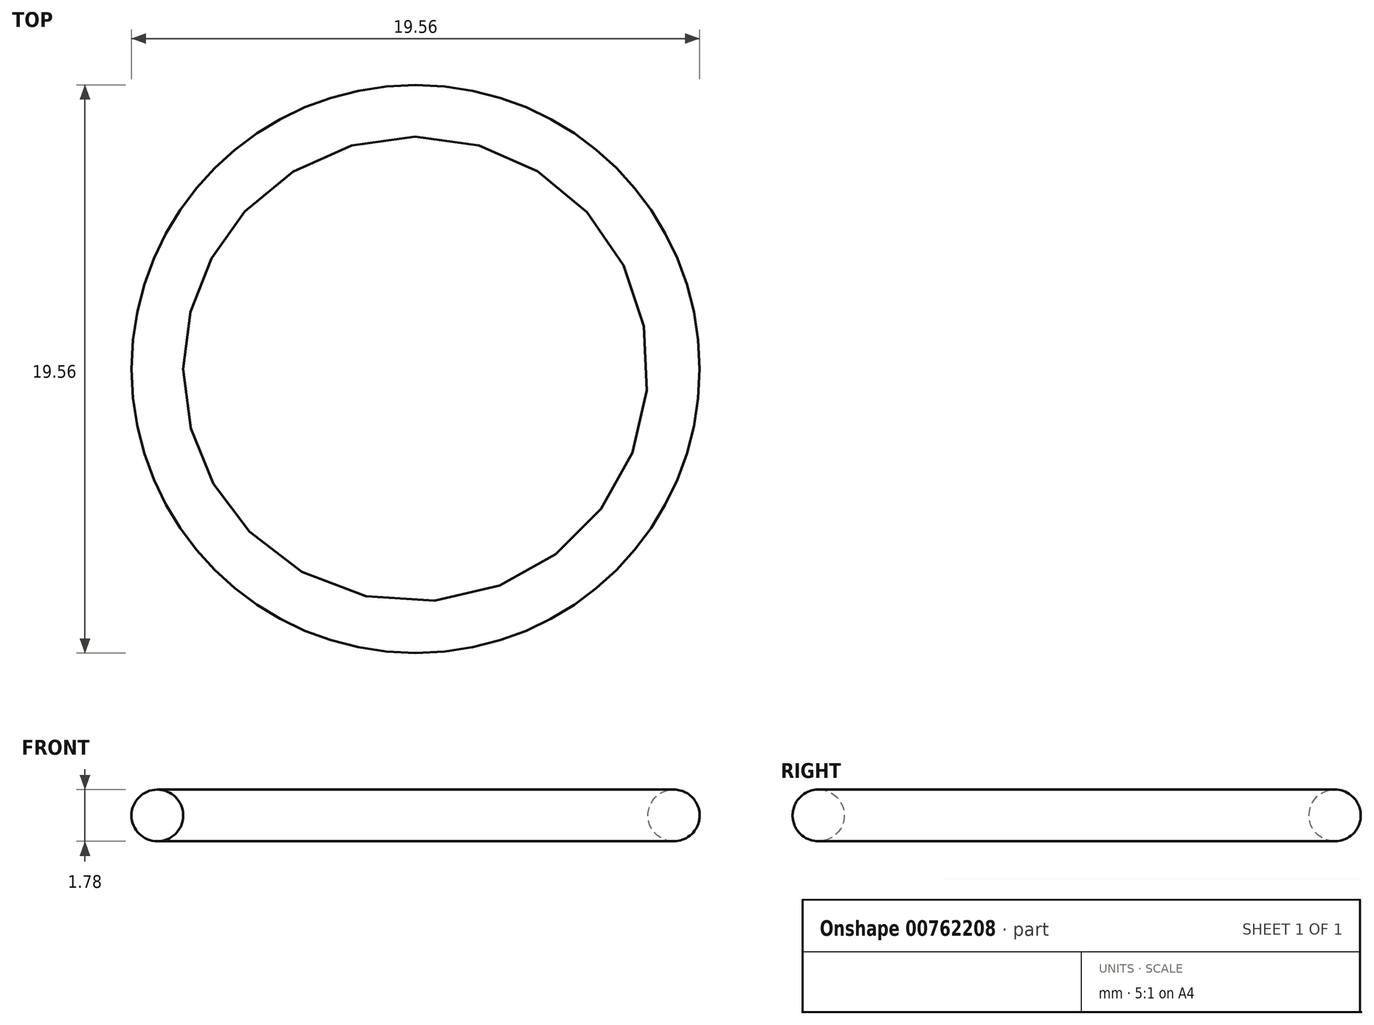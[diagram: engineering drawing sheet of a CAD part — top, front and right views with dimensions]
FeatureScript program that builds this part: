
annotation { "Feature Type Name" : "Feature", "Feature Type Description" : "" }
export const myFeature = defineFeature(function(context is Context, id is Id, definition is map)
    precondition{}
    {
        {
            var Q0;
            Q0=qCreatedBy(makeId("Right.planeOp"),FACE);
            var sketch = newSketch(context, id + "F0", { "sketchPlane" : qUnion([Q0])});
            skCircle(sketch, "E0", {"center": v(-8.9, 0) * mm, "radius": 0.89 * mm});
            skLineSegment(sketch, "E1", {"start": v(0, -2.68) * mm, "end": v(0, 2.47) * mm, "construction": true});
            skSolve(sketch);
        }
        {
            var Q0;
            Q0=makeQuery(id+"F0.imprint","IMPRINT",FACE,{"disambiguationData":[TD([[makeQuery(id+"F0.imprint","IMPRINT",EDGE,{"derivedFrom":sQuery(id+"F0.wireOp",EDGE,"E0")}),1.0]])]});
            var Q1;
            Q1=sQuery(id+"F0.wireOp",EDGE,"E1");
            revolve(context, id + "F1", {"surfaceOperationType" : NewSurfaceOperationType.NEW, "entities" : qUnion([Q0]), "axis" : qUnion([Q1]), "revolveType" : RevolveType.FULL});
        }
    });
